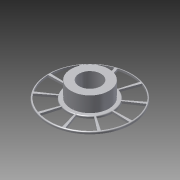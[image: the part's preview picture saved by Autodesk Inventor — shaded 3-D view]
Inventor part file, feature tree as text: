
AUTODESK INVENTOR PART (.ipt)
format: ipt  version: 2015 (Build 190159000, 159)  size: 324,608 bytes
history: native  units: mm
features: extrude x6, sketch x6, fillet x2
ambient origin geometry x8: Origin, YZ Plane, XZ Plane, XY Plane, X Axis, Y Axis, Z Axis, Center Point
bodies: Solid1 (feature_tree)
feature tree (14):
  extrude  "Main Body"  Depth=84.5mm
  extrude  "Indent (Deprecateds)"  Depth=5.0mm
  extrude  "Hub/Connector"  Depth=51.75mm
  extrude  "Cheap Hole Pattern"  Depth=84.5mm
  extrude  "InnerSpool"  Depth=54.243207mm
  fillet  "Outer Fillet"  Radius=41.0625mm
  fillet  "Inner Fillet"  Radius=54.243207mm
  extrude  "Filament Hole"  Depth=2.0mm TaperAngle=0.0deg
  sketch  "Sketch1"  dims[d0=200.0mm d1=84.5mm]
  sketch  "Sketch2"  dims[d2=5.0mm d3=0.0mm d4=90.5mm]
  sketch  "Sketch3"  dims[d5=16.0mm d6=0.0mm d7=51.75mm]
  sketch  "Sketch5"  dims[d8=20.5mm d9=0.0mm d10=84.5mm]
  sketch  "Sketch7"  dims[d11=90.5mm d34=194.0mm d36=41.0625mm d37=54.243207mm]
  sketch  "Sketch9"  dims[d38=100.0mm d40=360.0deg d42=68.0mm d43=0.0mm d44=21.0mm d45=0.0mm d47=150.0mm d48=2.5mm d49=5.0mm d50=10.0mm d51=13.0mm d52=7.5mm d53=15.0mm d54=360.0deg d55=41.375mm d56=25.0mm d57=0.0mm d58=2.0mm d59=2.0mm d65=2.0mm d66=14.0mm d67=0.0mm]
